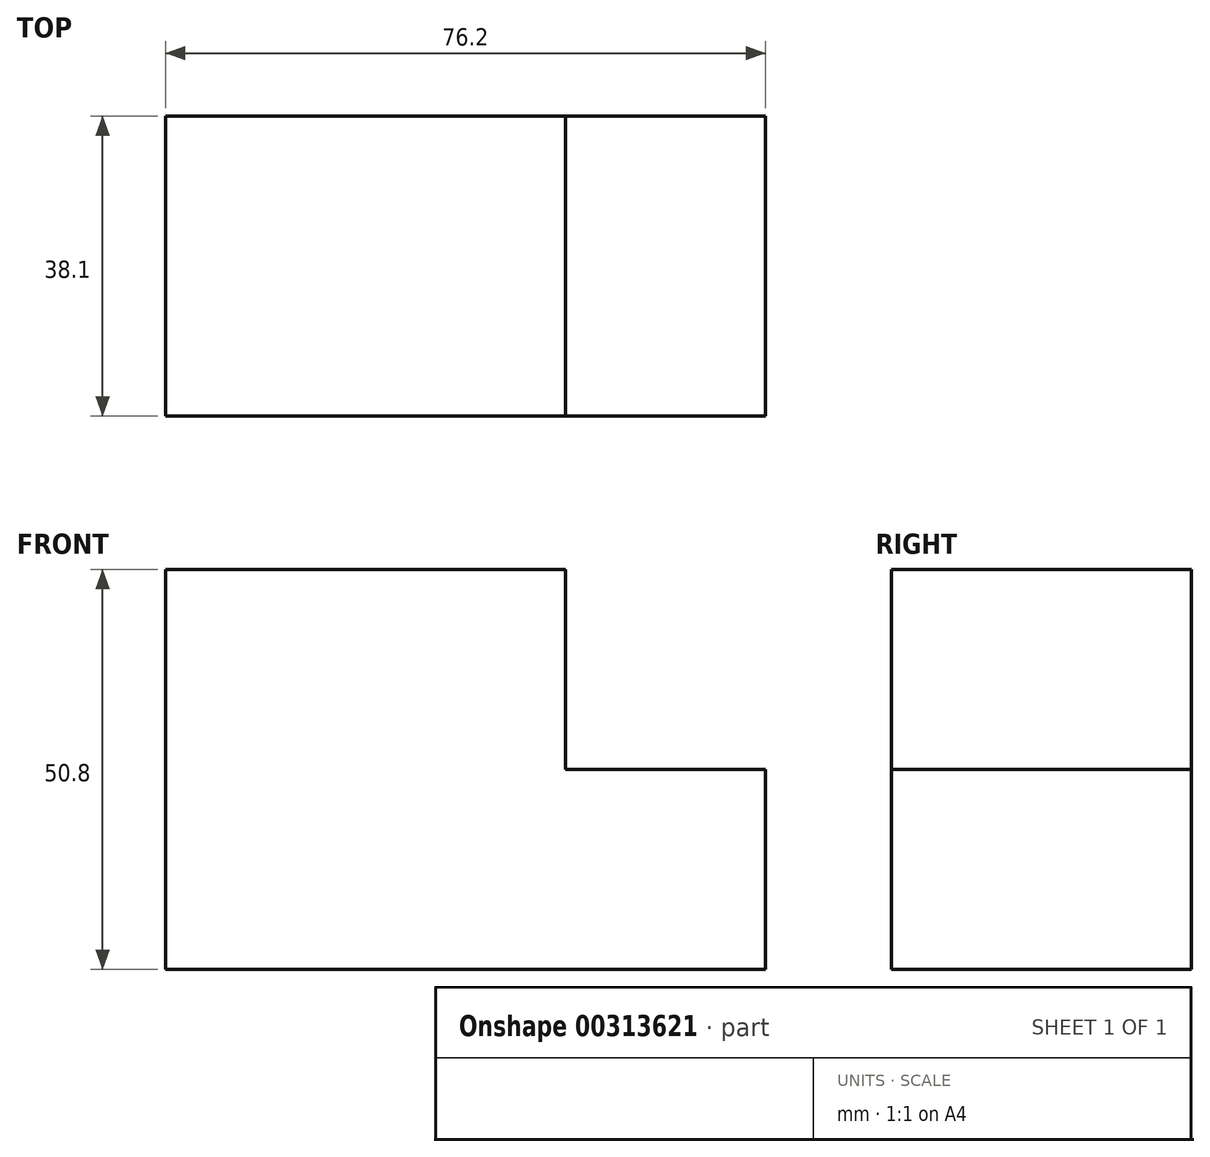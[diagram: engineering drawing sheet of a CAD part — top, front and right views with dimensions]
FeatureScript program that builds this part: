
annotation { "Feature Type Name" : "Feature", "Feature Type Description" : "" }
export const myFeature = defineFeature(function(context is Context, id is Id, definition is map)
    precondition{}
    {
        {
            var Q0;
            Q0=qCreatedBy(makeId("Front.planeOp"),FACE);
            var sketch = newSketch(context, id + "F0", { "sketchPlane" : qUnion([Q0])});
            skLineSegment(sketch, "E0", {"start": v(-39.66, -53.54) * mm, "end": v(36.54, -53.54) * mm});
            skLineSegment(sketch, "E1", {"start": v(36.54, -53.54) * mm, "end": v(36.54, -28.14) * mm});
            skLineSegment(sketch, "E2", {"start": v(36.54, -28.14) * mm, "end": v(11.14, -28.14) * mm});
            skLineSegment(sketch, "E3", {"start": v(-39.66, -53.54) * mm, "end": v(-39.66, -2.74) * mm});
            skLineSegment(sketch, "E4", {"start": v(-39.66, -2.74) * mm, "end": v(11.14, -2.74) * mm});
            skLineSegment(sketch, "E5", {"start": v(11.14, -2.74) * mm, "end": v(11.14, -28.14) * mm});
            skSolve(sketch);
        }
        {
            var Q0;
            Q0=makeQuery(id+"F0.imprint","IMPRINT",FACE,{"disambiguationData":[TD([[makeQuery(id+"F0.imprint","IMPRINT",EDGE,{"derivedFrom":sQuery(id+"F0.wireOp",EDGE,"E0")}),1.0]])]});
            extrude(context, id + "F1", {"entities" : qUnion([Q0]), "depth" : 38.1 * mm});
        }
    });
